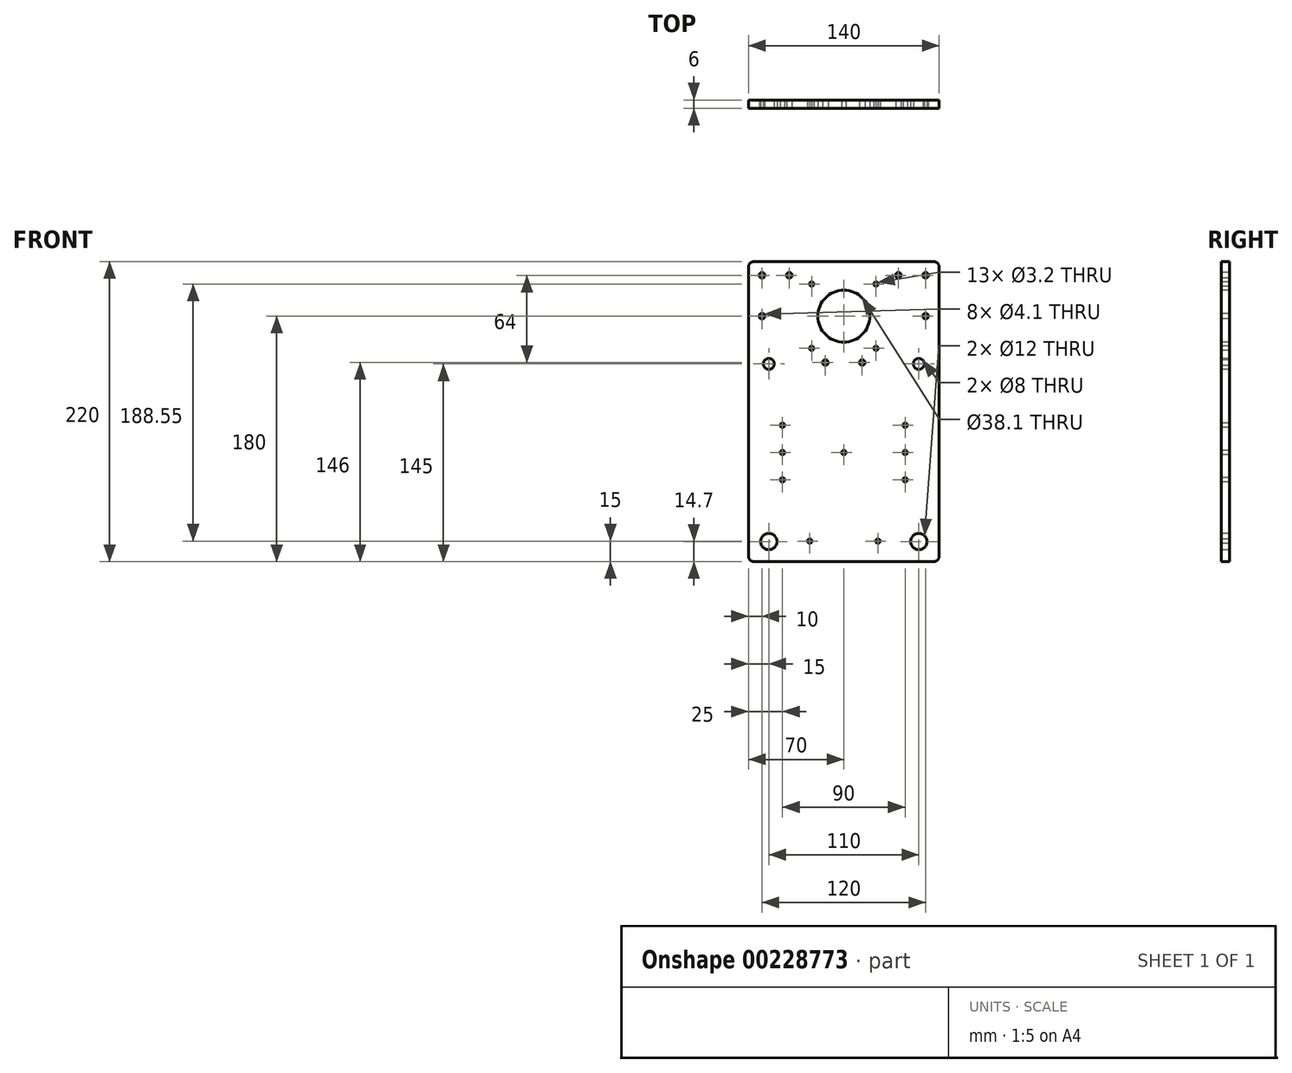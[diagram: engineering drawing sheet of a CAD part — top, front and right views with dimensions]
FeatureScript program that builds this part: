
annotation { "Feature Type Name" : "Feature", "Feature Type Description" : "" }
export const myFeature = defineFeature(function(context is Context, id is Id, definition is map)
    precondition{}
    {
        {
            var Q0;
            Q0=qCreatedBy(makeId("Front.planeOp"),FACE);
            var sketch = newSketch(context, id + "F0", { "sketchPlane" : qUnion([Q0])});
            skPoint(sketch, "E0.middle", {"position": v(0, 0) * mm});
            skLineSegment(sketch, "E1", {"start": v(-70, -80) * mm, "end": v(-70, 140) * mm});
            skLineSegment(sketch, "E2", {"start": v(-70, 140) * mm, "end": v(70, 140) * mm});
            skLineSegment(sketch, "E3", {"start": v(70, 140) * mm, "end": v(70, -80) * mm});
            skLineSegment(sketch, "E4", {"start": v(70, -80) * mm, "end": v(-70, -80) * mm});
            skLineSegment(sketch, "E5", {"start": v(-70, 0) * mm, "end": v(70, 0) * mm, "construction": true});
            skLineSegment(sketch, "E6", {"start": v(0, -80) * mm, "end": v(0, 140) * mm, "construction": true});
            skSolve(sketch);
        }
        {
            var Q0;
            Q0=makeQuery(id+"F0.imprint","IMPRINT",FACE,{"disambiguationData":[TD([[makeQuery(id+"F0.imprint","IMPRINT",EDGE,{"derivedFrom":sQuery(id+"F0.wireOp",EDGE,"E1")}),-1.0]])]});
            extrude(context, id + "F1", {"entities" : qUnion([Q0]), "depth" : 6 * mm});
        }
        {
            var Q0;
            Q0=makeQuery(id+"F1.opExtrude","CAP_FACE",FACE,{"disambiguationData":[OSD([sQuery(id+"F0.wireOp",EDGE,"E1"),sQuery(id+"F0.wireOp",EDGE,"E2"),sQuery(id+"F0.wireOp",EDGE,"E3"),sQuery(id+"F0.wireOp",EDGE,"E4")])],"isStart":false});
            var sketch = newSketch(context, id + "F2", { "sketchPlane" : qUnion([Q0])});
            skLineSegment(sketch, "E7", {"start": v(-70, 0) * mm, "end": v(70, 0) * mm, "construction": true});
            skLineSegment(sketch, "E8", {"start": v(0, 140) * mm, "end": v(0, -80) * mm, "construction": true});
            skCircle(sketch, "E9", {"center": v(-55, 65) * mm, "radius": 4 * mm});
            skCircle(sketch, "E10", {"center": v(55, 65) * mm, "radius": 4 * mm});
            skCircle(sketch, "E11", {"center": v(55, -65.3) * mm, "radius": 6 * mm});
            skCircle(sketch, "E12", {"center": v(-55, -65.3) * mm, "radius": 6 * mm});
            skCircle(sketch, "E13", {"center": v(0, 100) * mm, "radius": 19.05 * mm});
            skPoint(sketch, "E14", {"position": v(-23.55, 123.55) * mm});
            skPoint(sketch, "E15", {"position": v(23.55, 123.55) * mm});
            skPoint(sketch, "E16", {"position": v(23.55, 76.45) * mm});
            skPoint(sketch, "E17", {"position": v(-23.55, 76.45) * mm});
            skPoint(sketch, "E18", {"position": v(-13.5, 66) * mm});
            skPoint(sketch, "E19", {"position": v(13.5, 66) * mm});
            skSolve(sketch);
        }
        {
            var Q0;
            Q0=sQuery(id+"F2.wireOp",VERTEX,"E18");
            var Q1;
            Q1=sQuery(id+"F2.wireOp",VERTEX,"E19");
            var Q2;
            Q2=makeQuery(id+"F1.opExtrude","SWEPT_BODY",BODY,{"disambiguationData":[OSD([sQuery(id+"F0.wireOp",EDGE,"E1"),sQuery(id+"F0.wireOp",EDGE,"E2"),sQuery(id+"F0.wireOp",EDGE,"E3"),sQuery(id+"F0.wireOp",EDGE,"E4")])]});
            hole(context, id + "F3", {"style" : HoleStyle.SIMPLE, "endStyle" : HoleEndStyle.THROUGH, "standardTappedOrClearance" : lookupTablePath({ "standard" : "ISO", "engagement" : "75%", "pitch" : "0.9 mm", "size" : "M5", "type" : "Tapped" }), "standardBlindInLast" : lookupTablePath({ "standard" : "ISO", "engagement" : "75%", "pitch" : "0.9 mm", "size" : "M5", "type" : "Tapped" }), "holeDiameter" : 4.1 * mm, "locations" : qUnion([Q0, Q1]), "scope" : qUnion([Q2]), "isTappedThrough" : true, "showTappedDepth" : true});
        }
        {
            var Q0;
            Q0=sQuery(id+"F2.wireOp",VERTEX,"E14");
            var Q1;
            Q1=sQuery(id+"F2.wireOp",VERTEX,"E15");
            var Q2;
            Q2=sQuery(id+"F2.wireOp",VERTEX,"E16");
            var Q3;
            Q3=sQuery(id+"F2.wireOp",VERTEX,"E17");
            var Q4;
            Q4=makeQuery(id+"F1.opExtrude","SWEPT_BODY",BODY,{"disambiguationData":[OSD([sQuery(id+"F0.wireOp",EDGE,"E1"),sQuery(id+"F0.wireOp",EDGE,"E2"),sQuery(id+"F0.wireOp",EDGE,"E3"),sQuery(id+"F0.wireOp",EDGE,"E4")])]});
            hole(context, id + "F4", {"style" : HoleStyle.SIMPLE, "endStyle" : HoleEndStyle.THROUGH, "standardTappedOrClearance" : lookupTablePath({ "standard" : "ISO", "engagement" : "75%", "pitch" : "0.75 mm", "size" : "M4", "type" : "Tapped" }), "standardBlindInLast" : lookupTablePath({ "standard" : "ISO", "engagement" : "75%", "pitch" : "0.75 mm", "size" : "M4", "type" : "Tapped" }), "holeDiameter" : 3.2 * mm, "locations" : qUnion([Q0, Q1, Q2, Q3]), "scope" : qUnion([Q4]), "isTappedThrough" : true, "showTappedDepth" : true});
        }
        {
            var Q0;
            Q0=makeQuery(id+"F2.imprint","IMPRINT",FACE,{"disambiguationData":[TD([[makeQuery(id+"F2.imprint","IMPRINT",EDGE,{"derivedFrom":sQuery(id+"F2.wireOp",EDGE,"E13")}),1.0]])]});
            var Q1;
            Q1=makeQuery(id+"F2.imprint","IMPRINT",FACE,{"disambiguationData":[TD([[makeQuery(id+"F2.imprint","IMPRINT",EDGE,{"derivedFrom":sQuery(id+"F2.wireOp",EDGE,"E9")}),1.0]])]});
            var Q2;
            Q2=makeQuery(id+"F2.imprint","IMPRINT",FACE,{"disambiguationData":[TD([[makeQuery(id+"F2.imprint","IMPRINT",EDGE,{"derivedFrom":sQuery(id+"F2.wireOp",EDGE,"E10")}),1.0]])]});
            var Q3;
            Q3=makeQuery(id+"F2.imprint","IMPRINT",FACE,{"disambiguationData":[TD([[makeQuery(id+"F2.imprint","IMPRINT",EDGE,{"derivedFrom":sQuery(id+"F2.wireOp",EDGE,"E12")}),1.0]])]});
            var Q4;
            Q4=makeQuery(id+"F2.imprint","IMPRINT",FACE,{"disambiguationData":[TD([[makeQuery(id+"F2.imprint","IMPRINT",EDGE,{"derivedFrom":sQuery(id+"F2.wireOp",EDGE,"E11")}),1.0]])]});
            extrude(context, id + "F5", {"entities" : qUnion([Q0, Q1, Q2, Q3, Q4]), "operationType" : NewBodyOperationType.REMOVE, "endBound" : BoundingType.THROUGH_ALL, "oppositeDirection" : true, "depth" : 25 * mm});
        }
        {
            var Q0;
            Q0=makeQuery(id+"F1.opExtrude","SWEPT_EDGE",EDGE,{"disambiguationData":[OSD([sQuery(id+"F0.wireOp",EDGE,"E2"),sQuery(id+"F0.wireOp",EDGE,"E3")])]});
            var Q1;
            Q1=makeQuery(id+"F1.opExtrude","SWEPT_EDGE",EDGE,{"disambiguationData":[OSD([sQuery(id+"F0.wireOp",EDGE,"E1"),sQuery(id+"F0.wireOp",EDGE,"E2")])]});
            var Q2;
            Q2=makeQuery(id+"F1.opExtrude","SWEPT_EDGE",EDGE,{"disambiguationData":[OSD([sQuery(id+"F0.wireOp",EDGE,"E1"),sQuery(id+"F0.wireOp",EDGE,"E4")])]});
            var Q3;
            Q3=makeQuery(id+"F1.opExtrude","SWEPT_EDGE",EDGE,{"disambiguationData":[OSD([sQuery(id+"F0.wireOp",EDGE,"E3"),sQuery(id+"F0.wireOp",EDGE,"E4")])]});
            fillet(context, id + "F6", {"entities" : qUnion([Q0, Q1, Q2, Q3]), "radius" : 4 * mm, "tangentPropagation" : true, "allowEdgeOverflow" : false});
        }
        {
            var Q0;
            Q0=makeQuery(id+"F1.opExtrude","CAP_FACE",FACE,{"disambiguationData":[OSD([sQuery(id+"F0.wireOp",EDGE,"E1"),sQuery(id+"F0.wireOp",EDGE,"E2"),sQuery(id+"F0.wireOp",EDGE,"E3"),sQuery(id+"F0.wireOp",EDGE,"E4")])],"isStart":false});
            var sketch = newSketch(context, id + "F7", { "sketchPlane" : qUnion([Q0])});
            skPoint(sketch, "E20", {"position": v(-45, 0) * mm});
            skLineSegment(sketch, "E21", {"start": v(0, 134.45) * mm, "end": v(0, -80) * mm, "construction": true});
            skPoint(sketch, "E21.startSnap0", {"position": v(0, 140) * mm});
            skPoint(sketch, "E22.MirrorP", {"position": v(45, 0) * mm});
            skPoint(sketch, "E23", {"position": v(-60, 130) * mm});
            skPoint(sketch, "E24", {"position": v(-60, 100) * mm});
            skPoint(sketch, "E25.MirrorP", {"position": v(60, 130) * mm});
            skPoint(sketch, "E26.MirrorP", {"position": v(60, 100) * mm});
            skPoint(sketch, "E27", {"position": v(-45, 20) * mm});
            skPoint(sketch, "E28", {"position": v(-45, -20) * mm});
            skPoint(sketch, "E29.MirrorP", {"position": v(45, 20) * mm});
            skPoint(sketch, "E30.MirrorP", {"position": v(45, -20) * mm});
            skPoint(sketch, "E31", {"position": v(0, 0) * mm});
            skPoint(sketch, "E32", {"position": v(-40, 130) * mm});
            skPoint(sketch, "E33.MirrorP", {"position": v(40, 130) * mm});
            skPoint(sketch, "E34", {"position": v(-25, -65) * mm});
            skPoint(sketch, "E35.MirrorP", {"position": v(25, -65) * mm});
            skSolve(sketch);
        }
        {
            var Q0;
            Q0=sQuery(id+"F7.wireOp",VERTEX,"E27");
            var Q1;
            Q1=sQuery(id+"F7.wireOp",VERTEX,"E20");
            var Q2;
            Q2=sQuery(id+"F7.wireOp",VERTEX,"E28");
            var Q3;
            Q3=sQuery(id+"F7.wireOp",VERTEX,"E34");
            var Q4;
            Q4=sQuery(id+"F7.wireOp",VERTEX,"E35.MirrorP");
            var Q5;
            Q5=sQuery(id+"F7.wireOp",VERTEX,"E30.MirrorP");
            var Q6;
            Q6=sQuery(id+"F7.wireOp",VERTEX,"E22.MirrorP");
            var Q7;
            Q7=sQuery(id+"F7.wireOp",VERTEX,"E29.MirrorP");
            var Q8;
            Q8=sQuery(id+"F7.wireOp",VERTEX,"E31");
            var Q9;
            Q9=makeQuery(id+"F1.opExtrude","SWEPT_BODY",BODY,{"disambiguationData":[OSD([sQuery(id+"F0.wireOp",EDGE,"E1"),sQuery(id+"F0.wireOp",EDGE,"E2"),sQuery(id+"F0.wireOp",EDGE,"E3"),sQuery(id+"F0.wireOp",EDGE,"E4")])]});
            hole(context, id + "F8", {"style" : HoleStyle.SIMPLE, "endStyle" : HoleEndStyle.THROUGH, "standardTappedOrClearance" : lookupTablePath({ "standard" : "ISO", "engagement" : "75%", "pitch" : "0.75 mm", "size" : "M4", "type" : "Tapped" }), "standardBlindInLast" : lookupTablePath({ "standard" : "ISO", "engagement" : "75%", "pitch" : "0.75 mm", "size" : "M4", "type" : "Tapped" }), "holeDiameter" : 3.2 * mm, "locations" : qUnion([Q0, Q1, Q2, Q3, Q4, Q5, Q6, Q7, Q8]), "scope" : qUnion([Q9]), "isTappedThrough" : true, "showTappedDepth" : true});
        }
        {
            var Q0;
            Q0=sQuery(id+"F7.wireOp",VERTEX,"E23");
            var Q1;
            Q1=sQuery(id+"F7.wireOp",VERTEX,"E24");
            var Q2;
            Q2=sQuery(id+"F7.wireOp",VERTEX,"E25.MirrorP");
            var Q3;
            Q3=sQuery(id+"F7.wireOp",VERTEX,"E26.MirrorP");
            var Q4;
            Q4=sQuery(id+"F7.wireOp",VERTEX,"E32");
            var Q5;
            Q5=sQuery(id+"F7.wireOp",VERTEX,"E33.MirrorP");
            var Q6;
            Q6=makeQuery(id+"F1.opExtrude","SWEPT_BODY",BODY,{"disambiguationData":[OSD([sQuery(id+"F0.wireOp",EDGE,"E1"),sQuery(id+"F0.wireOp",EDGE,"E2"),sQuery(id+"F0.wireOp",EDGE,"E3"),sQuery(id+"F0.wireOp",EDGE,"E4")])]});
            hole(context, id + "F9", {"style" : HoleStyle.SIMPLE, "endStyle" : HoleEndStyle.THROUGH, "standardTappedOrClearance" : lookupTablePath({ "standard" : "ISO", "engagement" : "75%", "pitch" : "0.9 mm", "size" : "M5", "type" : "Tapped" }), "standardBlindInLast" : lookupTablePath({ "standard" : "ISO", "engagement" : "75%", "pitch" : "0.9 mm", "size" : "M5", "type" : "Tapped" }), "holeDiameter" : 4.1 * mm, "locations" : qUnion([Q0, Q1, Q2, Q3, Q4, Q5]), "scope" : qUnion([Q6]), "isTappedThrough" : true, "showTappedDepth" : true});
        }
    });
